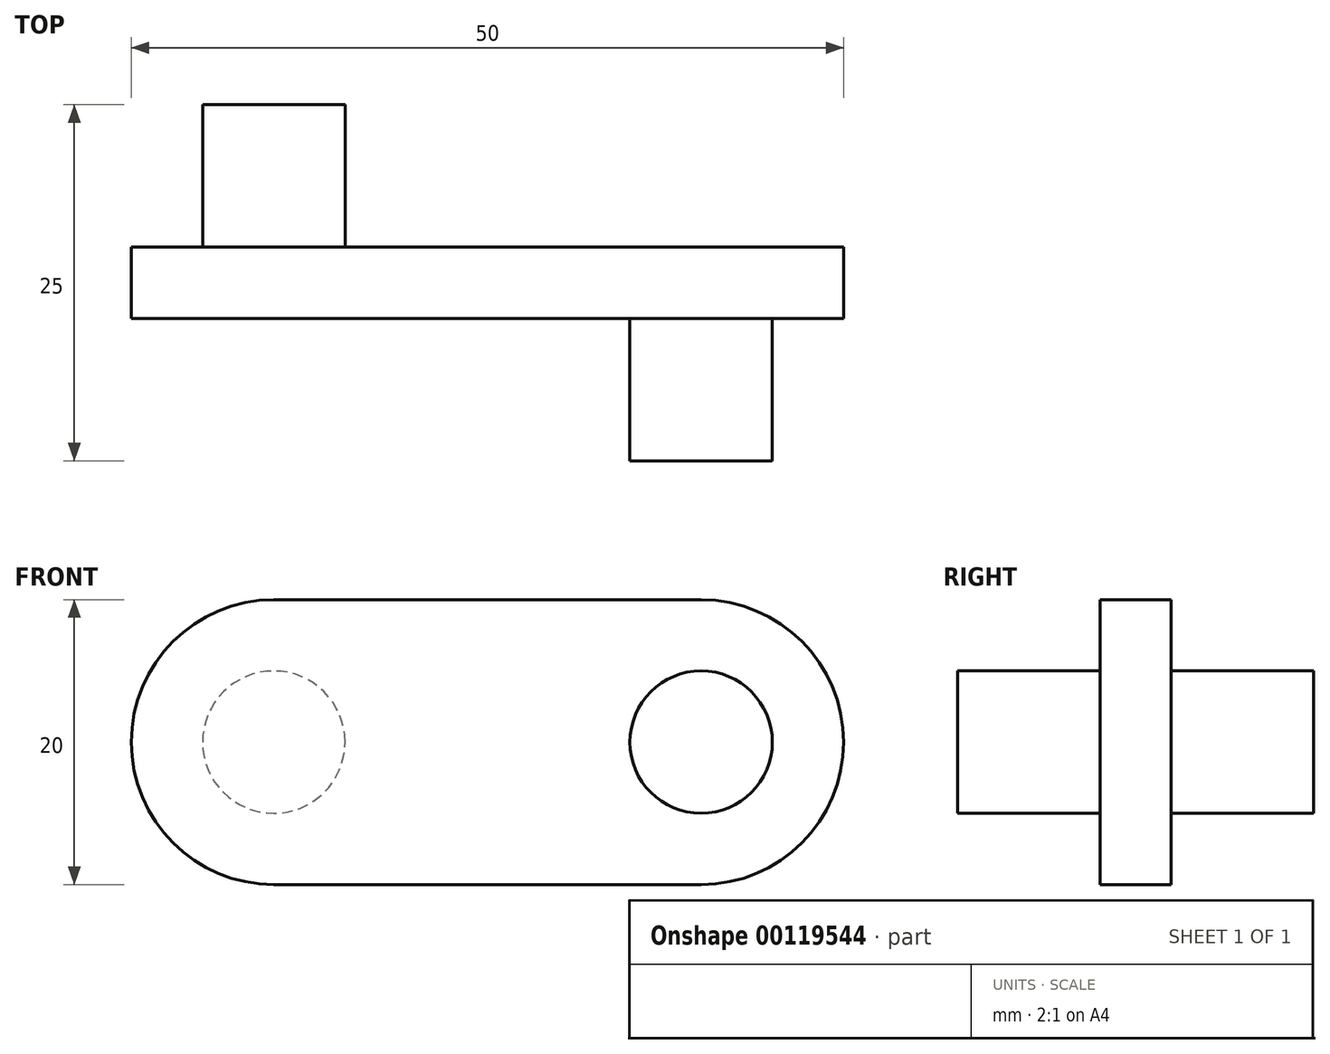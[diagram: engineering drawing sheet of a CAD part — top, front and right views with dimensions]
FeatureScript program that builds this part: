
annotation { "Feature Type Name" : "Feature", "Feature Type Description" : "" }
export const myFeature = defineFeature(function(context is Context, id is Id, definition is map)
    precondition{}
    {
        {
            var Q0;
            Q0=qCreatedBy(makeId("Front.planeOp"),FACE);
            var sketch = newSketch(context, id + "F0", { "sketchPlane" : qUnion([Q0])});
            skLineSegment(sketch, "E0.bottom", {"start": v(-15, -10) * mm, "end": v(15, -10) * mm});
            skLineSegment(sketch, "E0.top", {"start": v(-15, 10) * mm, "end": v(15, 10) * mm});
            skPoint(sketch, "E0.middle", {"position": v(0, 0) * mm});
            skCircle(sketch, "E1", {"center": v(-15, 0) * mm, "radius": 5 * mm});
            skCircle(sketch, "E2", {"center": v(15, 0) * mm, "radius": 5 * mm});
            skArc(sketch, "E3", {"start": v(-15, 10) * mm, "mid": v(-25, 0) * mm, "end": v(-15, -10) * mm});
            skArc(sketch, "E4", {"start": v(15, -10) * mm, "mid": v(25, 0) * mm, "end": v(15, 10) * mm});
            skSolve(sketch);
        }
        {
            var Q0;
            Q0=makeQuery(id+"F0.imprint","IMPRINT",FACE,{"disambiguationData":[TD([[makeQuery(id+"F0.imprint","IMPRINT",EDGE,{"derivedFrom":sQuery(id+"F0.wireOp",EDGE,"E0.bottom")}),1.0]])]});
            extrude(context, id + "F1", {"entities" : qUnion([Q0]), "depth" : 5 * mm});
        }
        {
            var Q0;
            Q0=makeQuery(id+"F0.imprint","IMPRINT",FACE,{"disambiguationData":[TD([[makeQuery(id+"F0.imprint","IMPRINT",EDGE,{"derivedFrom":sQuery(id+"F0.wireOp",EDGE,"E2")}),1.0]])]});
            extrude(context, id + "F2", {"entities" : qUnion([Q0]), "operationType" : NewBodyOperationType.ADD, "depth" : 15 * mm});
        }
        {
            var Q0;
            Q0=makeQuery(id+"F0.imprint","IMPRINT",FACE,{"disambiguationData":[TD([[makeQuery(id+"F0.imprint","IMPRINT",EDGE,{"derivedFrom":sQuery(id+"F0.wireOp",EDGE,"E1")}),1.0]])]});
            extrude(context, id + "F3", {"entities" : qUnion([Q0]), "operationType" : NewBodyOperationType.ADD, "oppositeDirection" : true, "depth" : 10 * mm, "hasSecondDirection" : true, "secondDirectionOppositeDirection" : false, "secondDirectionDepth" : 5 * mm});
        }
    });
